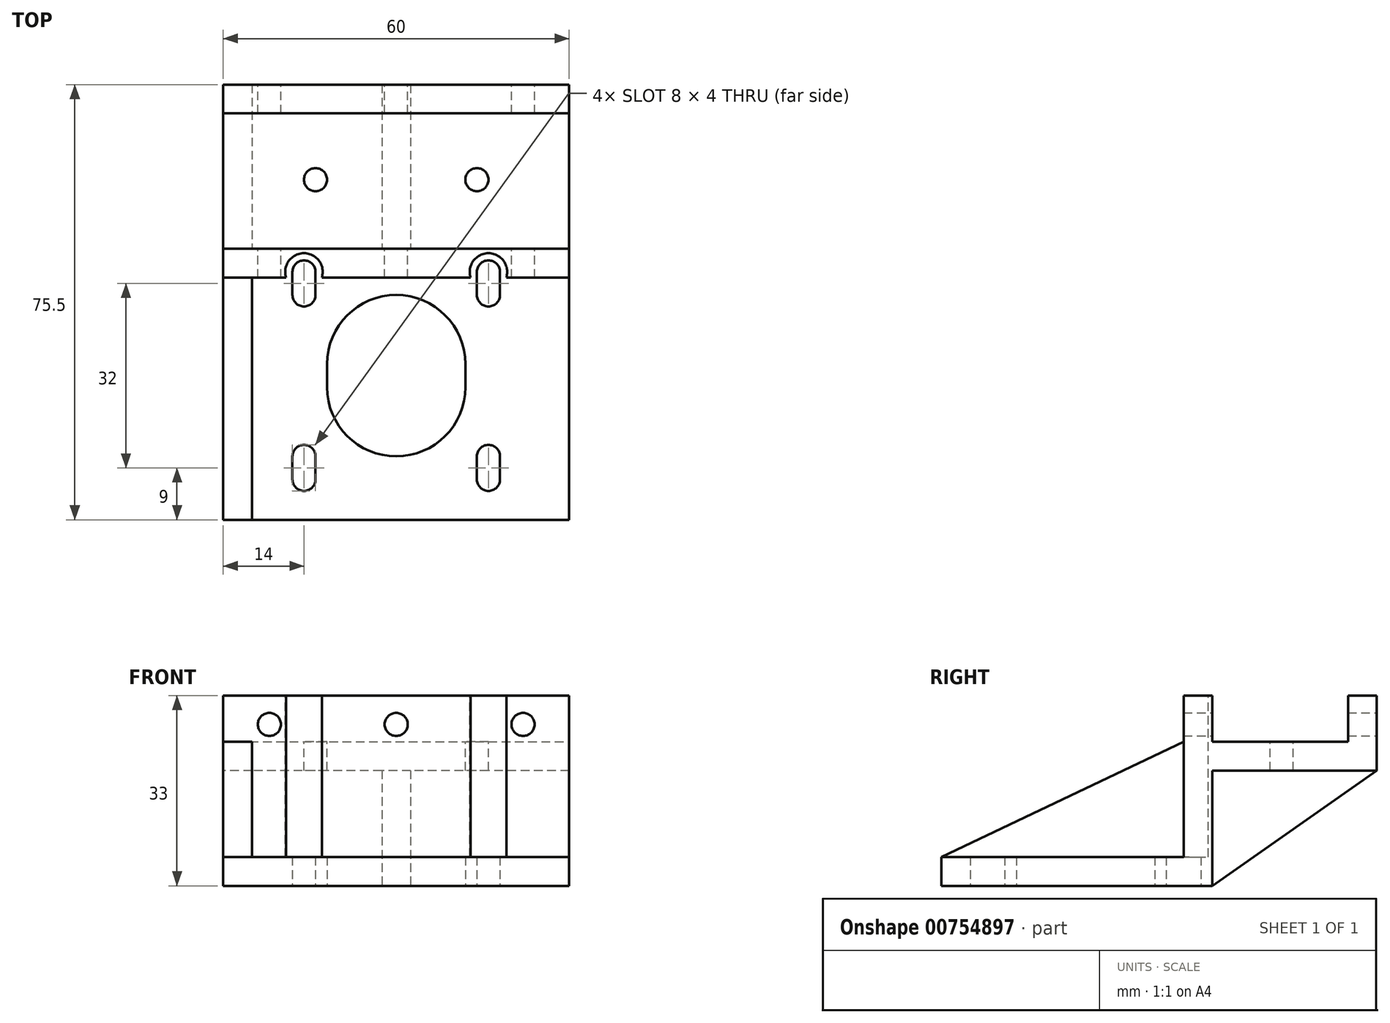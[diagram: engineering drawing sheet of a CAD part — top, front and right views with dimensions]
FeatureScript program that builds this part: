
annotation { "Feature Type Name" : "Feature", "Feature Type Description" : "" }
export const myFeature = defineFeature(function(context is Context, id is Id, definition is map)
    precondition{}
    {
        {
            var Q0;
            Q0=qCreatedBy(makeId("Top.planeOp"),FACE);
            var sketch = newSketch(context, id + "F0", { "sketchPlane" : qUnion([Q0])});
            skLineSegment(sketch, "E0.bottom", {"start": v(-30, 22) * mm, "end": v(30, 22) * mm});
            skLineSegment(sketch, "E0.top", {"start": v(-30, -25) * mm, "end": v(30, -25) * mm});
            skLineSegment(sketch, "E0.left", {"start": v(-30, 22) * mm, "end": v(-30, -25) * mm});
            skLineSegment(sketch, "E0.right", {"start": v(30, 22) * mm, "end": v(30, -25) * mm});
            skLineSegment(sketch, "E1", {"start": v(16, 18) * mm, "end": v(16, 14) * mm});
            skArc(sketch, "E2.0.startCap", {"start": v(14, 18) * mm, "mid": v(16, 20) * mm, "end": v(18, 18) * mm});
            skArc(sketch, "E2.0.endCap", {"start": v(18, 14) * mm, "mid": v(16, 12) * mm, "end": v(14, 14) * mm});
            skLineSegment(sketch, "E2.0.left", {"start": v(18, 18) * mm, "end": v(18, 14) * mm});
            skLineSegment(sketch, "E2.0.right", {"start": v(14, 18) * mm, "end": v(14, 14) * mm});
            skArc(sketch, "E3.2.0", {"start": v(-14, -18) * mm, "mid": v(-16, -20) * mm, "end": v(-18, -18) * mm});
            skLineSegment(sketch, "E3.2.1", {"start": v(-18, -18) * mm, "end": v(-18, -14) * mm});
            skLineSegment(sketch, "E3.2.2", {"start": v(-14, -18) * mm, "end": v(-14, -14) * mm});
            skArc(sketch, "E3.2.3", {"start": v(-18, -14) * mm, "mid": v(-16, -12) * mm, "end": v(-14, -14) * mm});
            skPoint(sketch, "E3.center", {"position": v(0, 0) * mm});
            skLineSegment(sketch, "E4.MirrorCS", {"start": v(18, -18) * mm, "end": v(18, -14) * mm});
            skArc(sketch, "E5.MirrorCS", {"start": v(18, -14) * mm, "mid": v(16, -12) * mm, "end": v(14, -14) * mm});
            skArc(sketch, "E6.MirrorCS", {"start": v(14, -18) * mm, "mid": v(16, -20) * mm, "end": v(18, -18) * mm});
            skLineSegment(sketch, "E7.MirrorCS", {"start": v(14, -18) * mm, "end": v(14, -14) * mm});
            skArc(sketch, "E8.MirrorCS", {"start": v(-18, 14) * mm, "mid": v(-16, 12) * mm, "end": v(-14, 14) * mm});
            skArc(sketch, "E9.MirrorCS", {"start": v(-14, 18) * mm, "mid": v(-16, 20) * mm, "end": v(-18, 18) * mm});
            skLineSegment(sketch, "E10.MirrorCS", {"start": v(-16, 18) * mm, "end": v(-16, 14) * mm});
            skLineSegment(sketch, "E11.MirrorCS", {"start": v(-18, 18) * mm, "end": v(-18, 14) * mm});
            skLineSegment(sketch, "E12.MirrorCS", {"start": v(-14, 18) * mm, "end": v(-14, 14) * mm});
            skLineSegment(sketch, "E13", {"start": v(0, 2) * mm, "end": v(0, -2) * mm});
            skArc(sketch, "E14.0.startCap", {"start": v(-12, 2) * mm, "mid": v(0, 14) * mm, "end": v(12, 2) * mm});
            skArc(sketch, "E14.0.endCap", {"start": v(12, -2) * mm, "mid": v(0, -14) * mm, "end": v(-12, -2) * mm});
            skLineSegment(sketch, "E14.0.left", {"start": v(12, 2) * mm, "end": v(12, -2) * mm});
            skLineSegment(sketch, "E14.0.right", {"start": v(-12, 2) * mm, "end": v(-12, -2) * mm});
            skSolve(sketch);
        }
        {
            var Q0;
            Q0 = qSketchRegion(id + "F0", true);
            extrude(context, id + "F1", {"entities" : qUnion([Q0]), "depth" : 5 * mm, "offsetDistance" : 25 * mm});
        }
        {
            var Q0;
            Q0=makeQuery(id+"F1.opExtrude","CAP_FACE",FACE,{"disambiguationData":[OSD([sQuery(id+"F0.wireOp",EDGE,"E0.bottom"),sQuery(id+"F0.wireOp",EDGE,"E0.top"),sQuery(id+"F0.wireOp",EDGE,"E0.left"),sQuery(id+"F0.wireOp",EDGE,"E0.right"),sQuery(id+"F0.wireOp",EDGE,"ebf0b98d-d063-4ffa-b0bc-1d316e2de7a7"),sQuery(id+"F0.wireOp",EDGE,"e8bd3b5a-af89-4b67-b91b-1c70ef5e374c"),sQuery(id+"F0.wireOp",EDGE,"afbd3648-d512-4112-9934-f4e6d17edb44"),sQuery(id+"F0.wireOp",EDGE,"97d7f5a2-a687-41cf-9236-51411ab76abc"),sQuery(id+"F0.wireOp",EDGE,"c5fa1335-ed47-46ac-8785-0048e36bfd22")])],"isStart":false});
            var sketch = newSketch(context, id + "F2", { "sketchPlane" : qUnion([Q0])});
            skLineSegment(sketch, "E15.bottom", {"start": v(-30, 22) * mm, "end": v(30, 22) * mm});
            skLineSegment(sketch, "E15.top", {"start": v(-30, 17) * mm, "end": v(30, 17) * mm});
            skLineSegment(sketch, "E15.left", {"start": v(-30, 22) * mm, "end": v(-30, 17) * mm});
            skLineSegment(sketch, "E15.right", {"start": v(30, 22) * mm, "end": v(30, 17) * mm});
            skSolve(sketch);
        }
        {
            var Q0;
            Q0=makeQuery(id+"F2.imprint","IMPRINT",FACE,{"disambiguationData":[TD([[makeQuery(id+"F2.imprint","IMPRINT",EDGE,{"derivedFrom":sQuery(id+"F2.wireOp",EDGE,"E15.bottom")}),-1.0]])]});
            extrude(context, id + "F3", {"entities" : qUnion([Q0]), "operationType" : NewBodyOperationType.ADD, "depth" : 20 * mm, "offsetDistance" : 25 * mm});
        }
        {
            var Q0;
            Q0=makeQuery(id+"F3.boolean.opBoolean","MERGE",FACE,{"derivedFrom":[makeQuery(id+"F1.opExtrude","SWEPT_FACE",FACE,{"disambiguationData":[OSD([sQuery(id+"F0.wireOp",EDGE,"E0.bottom")])]}),makeQuery(id+"F3.opExtrude","SWEPT_FACE",FACE,{"disambiguationData":[OSD([sQuery(id+"F2.wireOp",EDGE,"E15.bottom")])]})]});
            var sketch = newSketch(context, id + "F4", { "sketchPlane" : qUnion([Q0])});
            skLineSegment(sketch, "E16.bottom", {"start": v(-30, 25) * mm, "end": v(30, 25) * mm});
            skLineSegment(sketch, "E16.top", {"start": v(-30, 20) * mm, "end": v(30, 20) * mm});
            skLineSegment(sketch, "E16.left", {"start": v(-30, 25) * mm, "end": v(-30, 20) * mm});
            skLineSegment(sketch, "E16.right", {"start": v(30, 25) * mm, "end": v(30, 20) * mm});
            skSolve(sketch);
        }
        {
            var Q0;
            Q0=makeQuery(id+"F4.imprint","IMPRINT",FACE,{"disambiguationData":[TD([[makeQuery(id+"F4.imprint","IMPRINT",EDGE,{"derivedFrom":sQuery(id+"F4.wireOp",EDGE,"E16.bottom")}),1.0]])]});
            extrude(context, id + "F5", {"entities" : qUnion([Q0]), "operationType" : NewBodyOperationType.ADD, "depth" : 28.5 * mm, "offsetDistance" : 25 * mm});
        }
        {
            var Q0;
            Q0=makeQuery(id+"F5.boolean.opBoolean","MERGE",FACE,{"derivedFrom":[makeQuery(id+"F3.boolean.opBoolean","MERGE",FACE,{"derivedFrom":[makeQuery(id+"F1.opExtrude","SWEPT_FACE",FACE,{"disambiguationData":[OSD([sQuery(id+"F0.wireOp",EDGE,"E0.left")])]}),makeQuery(id+"F3.opExtrude","SWEPT_FACE",FACE,{"disambiguationData":[OSD([sQuery(id+"F2.wireOp",EDGE,"E15.left")])]})]}),makeQuery(id+"F5.opExtrude","SWEPT_FACE",FACE,{"disambiguationData":[OSD([sQuery(id+"F4.wireOp",EDGE,"E16.right")])]})]});
            var sketch = newSketch(context, id + "F6", { "sketchPlane" : qUnion([Q0])});
            skLineSegment(sketch, "E17", {"start": v(-50.5, 20) * mm, "end": v(-22, 20) * mm});
            skLineSegment(sketch, "E18", {"start": v(-22, 20) * mm, "end": v(-22, 0) * mm});
            skLineSegment(sketch, "E19", {"start": v(-22, 0) * mm, "end": v(-50.5, 20) * mm});
            skLineSegment(sketch, "E20", {"start": v(-17, 25) * mm, "end": v(-17, 5) * mm});
            skLineSegment(sketch, "E21", {"start": v(-17, 5) * mm, "end": v(25, 5) * mm});
            skLineSegment(sketch, "E22", {"start": v(25, 5) * mm, "end": v(-17, 25) * mm});
            skSolve(sketch);
        }
        {
            var Q0;
            Q0 = qSketchRegion(id + "F6", true);
            extrude(context, id + "F7", {"entities" : qUnion([Q0]), "operationType" : NewBodyOperationType.ADD, "oppositeDirection" : true, "depth" : 5 * mm, "offsetDistance" : 25 * mm});
        }
        {
            var Q0;
            Q0=makeQuery(id+"F5.boolean.opBoolean","MERGE",FACE,{"derivedFrom":[makeQuery(id+"F3.opExtrude","CAP_FACE",FACE,{"disambiguationData":[OSD([sQuery(id+"F2.wireOp",EDGE,"E15.bottom"),sQuery(id+"F2.wireOp",EDGE,"E15.top"),sQuery(id+"F2.wireOp",EDGE,"E15.left"),sQuery(id+"F2.wireOp",EDGE,"E15.right")])],"isStart":false}),makeQuery(id+"F5.opExtrude","SWEPT_FACE",FACE,{"disambiguationData":[OSD([sQuery(id+"F4.wireOp",EDGE,"E16.bottom")])]})]});
            var sketch = newSketch(context, id + "F8", { "sketchPlane" : qUnion([Q0])});
            skLineSegment(sketch, "E23.bottom", {"start": v(-30, 22) * mm, "end": v(30, 22) * mm});
            skLineSegment(sketch, "E23.top", {"start": v(-30, 17) * mm, "end": v(30, 17) * mm});
            skLineSegment(sketch, "E23.left", {"start": v(-30, 22) * mm, "end": v(-30, 17) * mm});
            skLineSegment(sketch, "E23.right", {"start": v(30, 22) * mm, "end": v(30, 17) * mm});
            skSolve(sketch);
        }
        {
            var Q0;
            Q0=makeQuery(id+"F8.imprint","IMPRINT",FACE,{"disambiguationData":[TD([[makeQuery(id+"F8.imprint","IMPRINT",EDGE,{"derivedFrom":sQuery(id+"F8.wireOp",EDGE,"E23.bottom")}),-1.0]])]});
            extrude(context, id + "F9", {"entities" : qUnion([Q0]), "operationType" : NewBodyOperationType.ADD, "depth" : 8 * mm, "offsetDistance" : 25 * mm});
        }
        {
            var Q0;
            Q0=makeQuery(id+"F5.boolean.opBoolean","MERGE",FACE,{"derivedFrom":[makeQuery(id+"F3.opExtrude","CAP_FACE",FACE,{"disambiguationData":[OSD([sQuery(id+"F2.wireOp",EDGE,"E15.bottom"),sQuery(id+"F2.wireOp",EDGE,"E15.top"),sQuery(id+"F2.wireOp",EDGE,"E15.left"),sQuery(id+"F2.wireOp",EDGE,"E15.right")])],"isStart":false}),makeQuery(id+"F5.opExtrude","SWEPT_FACE",FACE,{"disambiguationData":[OSD([sQuery(id+"F4.wireOp",EDGE,"E16.bottom")])]})]});
            var sketch = newSketch(context, id + "F10", { "sketchPlane" : qUnion([Q0])});
            skLineSegment(sketch, "E24.bottom", {"start": v(-30, 50.5) * mm, "end": v(30, 50.5) * mm});
            skLineSegment(sketch, "E24.top", {"start": v(-30, 45.5) * mm, "end": v(30, 45.5) * mm});
            skLineSegment(sketch, "E24.left", {"start": v(-30, 50.5) * mm, "end": v(-30, 45.5) * mm});
            skLineSegment(sketch, "E24.right", {"start": v(30, 50.5) * mm, "end": v(30, 45.5) * mm});
            skSolve(sketch);
        }
        {
            var Q0;
            Q0=makeQuery(id+"F10.imprint","IMPRINT",FACE,{"disambiguationData":[TD([[makeQuery(id+"F10.imprint","IMPRINT",EDGE,{"derivedFrom":sQuery(id+"F10.wireOp",EDGE,"E24.bottom")}),-1.0]])]});
            extrude(context, id + "F11", {"entities" : qUnion([Q0]), "operationType" : NewBodyOperationType.ADD, "depth" : 8 * mm, "offsetDistance" : 25 * mm});
        }
        {
            var Q0;
            Q0=makeQuery(id+"F5.boolean.opBoolean","MERGE",FACE,{"derivedFrom":[makeQuery(id+"F3.opExtrude","CAP_FACE",FACE,{"disambiguationData":[OSD([sQuery(id+"F2.wireOp",EDGE,"E15.bottom"),sQuery(id+"F2.wireOp",EDGE,"E15.top"),sQuery(id+"F2.wireOp",EDGE,"E15.left"),sQuery(id+"F2.wireOp",EDGE,"E15.right")])],"isStart":false}),makeQuery(id+"F5.opExtrude","SWEPT_FACE",FACE,{"disambiguationData":[OSD([sQuery(id+"F4.wireOp",EDGE,"E16.bottom")])]})]});
            var sketch = newSketch(context, id + "F12", { "sketchPlane" : qUnion([Q0])});
            skCircle(sketch, "E25", {"center": v(-14, 34) * mm, "radius": 2 * mm});
            skCircle(sketch, "E26", {"center": v(14, 34) * mm, "radius": 2 * mm});
            skSolve(sketch);
        }
        {
            var Q0;
            Q0=makeQuery(id+"F12.imprint","IMPRINT",FACE,{"disambiguationData":[TD([[makeQuery(id+"F12.imprint","IMPRINT",EDGE,{"derivedFrom":sQuery(id+"F12.wireOp",EDGE,"E26")}),1.0]])]});
            var Q1;
            Q1=makeQuery(id+"F12.imprint","IMPRINT",FACE,{"disambiguationData":[TD([[makeQuery(id+"F12.imprint","IMPRINT",EDGE,{"derivedFrom":sQuery(id+"F12.wireOp",EDGE,"cKoycXaf-tpRF-NhQF-AUWp-koFJBvnYuwvO")}),1.0]])]});
            var Q2;
            Q2=makeQuery(id+"F12.imprint","IMPRINT",FACE,{"disambiguationData":[TD([[makeQuery(id+"F12.imprint","IMPRINT",EDGE,{"derivedFrom":sQuery(id+"F12.wireOp",EDGE,"E25")}),1.0]])]});
            extrude(context, id + "F13", {"entities" : qUnion([Q0, Q1, Q2]), "operationType" : NewBodyOperationType.REMOVE, "oppositeDirection" : true, "depth" : 25 * mm, "offsetDistance" : 25 * mm});
        }
        {
            var Q0;
            Q0=qCreatedBy(makeId("Right.planeOp"),FACE);
            var sketch = newSketch(context, id + "F14", { "sketchPlane" : qUnion([Q0])});
            skLineSegment(sketch, "E27.0.0", {"start": v(22, 0) * mm, "end": v(50.5, 20) * mm});
            skLineSegment(sketch, "E27.0.1", {"start": v(50.5, 20) * mm, "end": v(22, 20) * mm});
            skLineSegment(sketch, "E27.0.2", {"start": v(22, 20) * mm, "end": v(22, 0) * mm});
            skSolve(sketch);
        }
        {
            var Q0;
            Q0 = qSketchRegion(id + "F14", true);
            extrude(context, id + "F15", {"entities" : qUnion([Q0]), "operationType" : NewBodyOperationType.ADD, "depth" : 2.5 * mm, "offsetDistance" : 25 * mm, "hasSecondDirection" : true, "secondDirectionOppositeDirection" : true, "secondDirectionDepth" : 2.5 * mm});
        }
        {
            var Q0;
            Q0=makeQuery(id+"F11.boolean.opBoolean","MERGE",FACE,{"derivedFrom":[makeQuery(id+"F5.opExtrude","CAP_FACE",FACE,{"disambiguationData":[OSD([sQuery(id+"F4.wireOp",EDGE,"E16.bottom"),sQuery(id+"F4.wireOp",EDGE,"E16.top"),sQuery(id+"F4.wireOp",EDGE,"E16.left"),sQuery(id+"F4.wireOp",EDGE,"E16.right")])],"isStart":false}),makeQuery(id+"F11.opExtrude","SWEPT_FACE",FACE,{"disambiguationData":[OSD([sQuery(id+"F10.wireOp",EDGE,"E24.bottom")])]})]});
            var sketch = newSketch(context, id + "F16", { "sketchPlane" : qUnion([Q0])});
            skCircle(sketch, "E28", {"center": v(-22, 28) * mm, "radius": 2 * mm});
            skCircle(sketch, "E29", {"center": v(22, 28) * mm, "radius": 2 * mm});
            skCircle(sketch, "E30", {"center": v(0, 28) * mm, "radius": 2 * mm});
            skSolve(sketch);
        }
        {
            var Q0;
            Q0 = qSketchRegion(id + "F16", true);
            extrude(context, id + "F17", {"entities" : qUnion([Q0]), "operationType" : NewBodyOperationType.REMOVE, "endBound" : BoundingType.THROUGH_ALL, "oppositeDirection" : true, "depth" : 25 * mm, "offsetDistance" : 25 * mm});
        }
        {
            var Q0;
            Q0=makeQuery(id+"F9.opExtrude","CAP_FACE",FACE,{"disambiguationData":[OSD([sQuery(id+"F0.wireOp",EDGE,"E2.0.startCap"),sQuery(id+"F0.wireOp",EDGE,"E2.0.left"),sQuery(id+"F0.wireOp",EDGE,"E2.0.right"),sQuery(id+"F0.wireOp",EDGE,"E9.MirrorCS"),sQuery(id+"F0.wireOp",EDGE,"E11.MirrorCS"),sQuery(id+"F0.wireOp",EDGE,"E12.MirrorCS"),sQuery(id+"F8.wireOp",EDGE,"E23.bottom"),sQuery(id+"F8.wireOp",EDGE,"E23.top"),sQuery(id+"F8.wireOp",EDGE,"E23.left"),sQuery(id+"F8.wireOp",EDGE,"E23.right")])],"isStart":false});
            var sketch = newSketch(context, id + "F18", { "sketchPlane" : qUnion([Q0])});
            skCircle(sketch, "E31", {"center": v(-16, 18) * mm, "radius": 3.25 * mm});
            skCircle(sketch, "E32", {"center": v(16, 18) * mm, "radius": 3.25 * mm});
            skSolve(sketch);
        }
        {
            var Q0;
            Q0 = qSketchRegion(id + "F18", true);
            var Q1;
            Q1=makeQuery(id+"F1.opExtrude","CAP_FACE",FACE,{"disambiguationData":[OSD([sQuery(id+"F0.wireOp",EDGE,"E0.bottom"),sQuery(id+"F0.wireOp",EDGE,"E0.top"),sQuery(id+"F0.wireOp",EDGE,"E0.left"),sQuery(id+"F0.wireOp",EDGE,"E0.right"),sQuery(id+"F0.wireOp",EDGE,"E2.0.startCap"),sQuery(id+"F0.wireOp",EDGE,"E2.0.endCap"),sQuery(id+"F0.wireOp",EDGE,"E2.0.left"),sQuery(id+"F0.wireOp",EDGE,"E2.0.right"),sQuery(id+"F0.wireOp",EDGE,"E3.2.0"),sQuery(id+"F0.wireOp",EDGE,"E3.2.1"),sQuery(id+"F0.wireOp",EDGE,"E3.2.2"),sQuery(id+"F0.wireOp",EDGE,"E3.2.3"),sQuery(id+"F0.wireOp",EDGE,"E4.MirrorCS"),sQuery(id+"F0.wireOp",EDGE,"E5.MirrorCS"),sQuery(id+"F0.wireOp",EDGE,"E6.MirrorCS"),sQuery(id+"F0.wireOp",EDGE,"E7.MirrorCS"),sQuery(id+"F0.wireOp",EDGE,"E8.MirrorCS"),sQuery(id+"F0.wireOp",EDGE,"E9.MirrorCS"),sQuery(id+"F0.wireOp",EDGE,"E11.MirrorCS"),sQuery(id+"F0.wireOp",EDGE,"E12.MirrorCS"),sQuery(id+"F0.wireOp",EDGE,"E14.0.startCap"),sQuery(id+"F0.wireOp",EDGE,"E14.0.endCap"),sQuery(id+"F0.wireOp",EDGE,"E14.0.left"),sQuery(id+"F0.wireOp",EDGE,"E14.0.right")])],"isStart":false});
            extrude(context, id + "F19", {"entities" : qUnion([Q0]), "operationType" : NewBodyOperationType.REMOVE, "endBound" : BoundingType.UP_TO_SURFACE, "oppositeDirection" : true, "depth" : 25 * mm, "endBoundEntityFace" : qUnion([Q1]), "offsetDistance" : 25 * mm});
        }
        {
            var Q0;
            Q0 = qSketchRegion(id + "F16", true);
            extrude(context, id + "F20", {"entities" : qUnion([Q0]), "operationType" : NewBodyOperationType.REMOVE, "endBound" : BoundingType.THROUGH_ALL, "depth" : 25 * mm, "offsetDistance" : 25 * mm});
        }
    });
